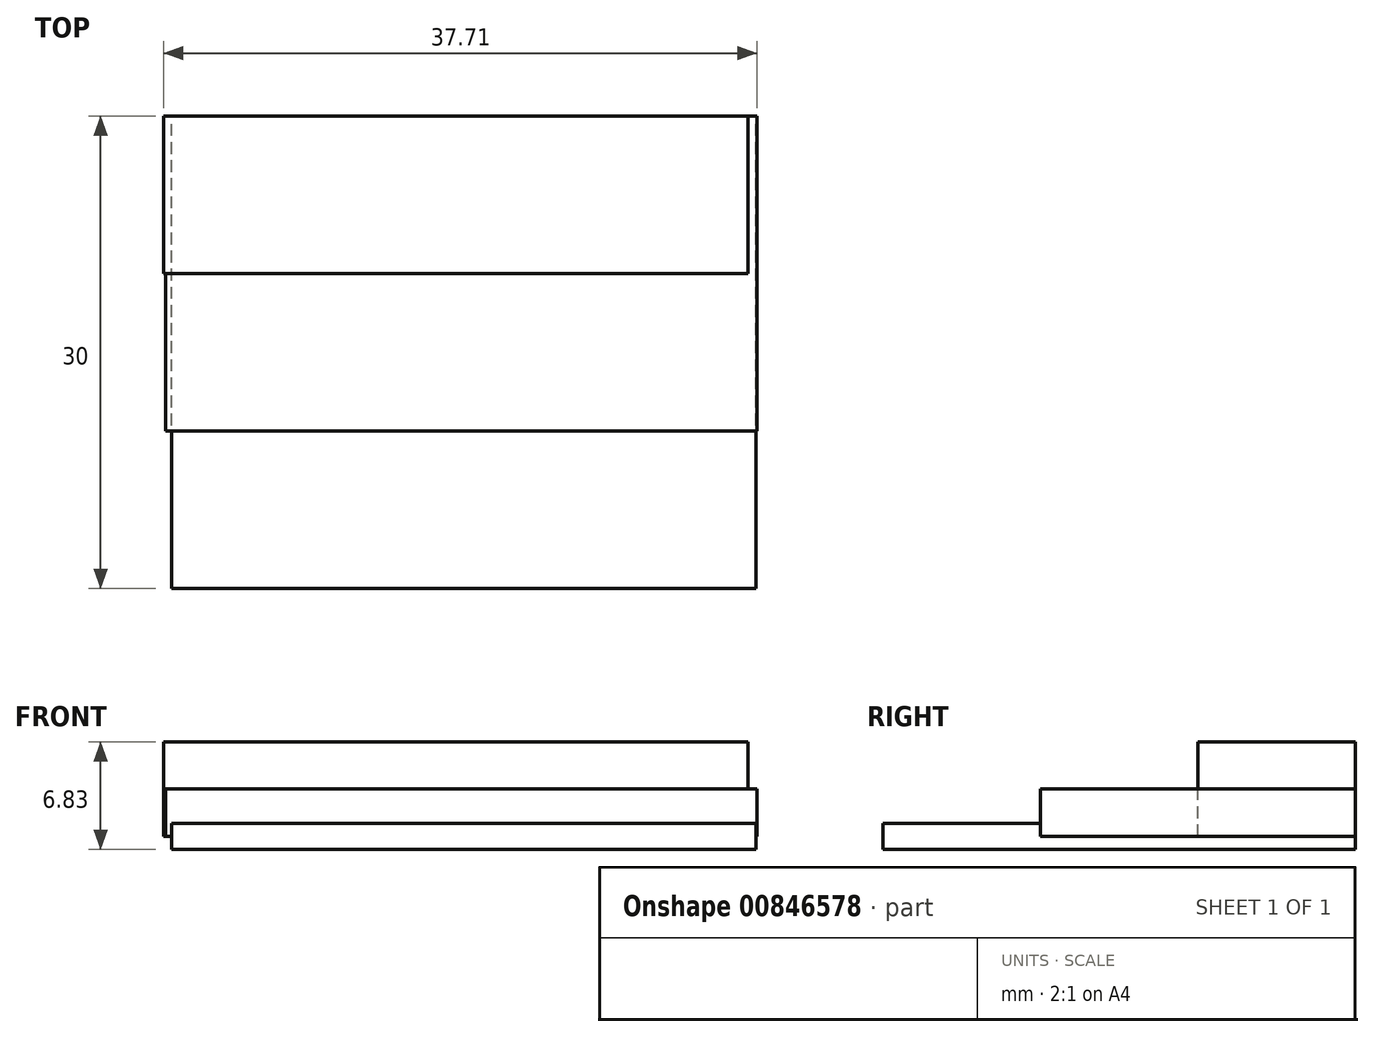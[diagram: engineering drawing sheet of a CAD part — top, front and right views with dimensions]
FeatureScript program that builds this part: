
annotation { "Feature Type Name" : "Feature", "Feature Type Description" : "" }
export const myFeature = defineFeature(function(context is Context, id is Id, definition is map)
    precondition{}
    {
        {
            var Q0;
            Q0=qCreatedBy(makeId("Front.planeOp"),FACE);
            var sketch = newSketch(context, id + "F0", { "sketchPlane" : qUnion([Q0])});
            skLineSegment(sketch, "E0.bottom", {"start": v(-15.71, 0.83) * mm, "end": v(21.43, 0.83) * mm});
            skLineSegment(sketch, "E0.top", {"start": v(-15.71, -0.83) * mm, "end": v(21.43, -0.83) * mm});
            skLineSegment(sketch, "E0.left", {"start": v(-15.71, 0.83) * mm, "end": v(-15.71, -0.83) * mm});
            skLineSegment(sketch, "E0.right", {"start": v(21.43, 0.83) * mm, "end": v(21.43, -0.83) * mm});
            skPoint(sketch, "E0.middle", {"position": v(2.86, 0) * mm});
            skSolve(sketch);
        }
        {
            var Q0;
            Q0 = qSketchRegion(id + "F0", true);
            extrude(context, id + "F1", {"entities" : qUnion([Q0]), "depth" : 30 * mm, "offsetDistance" : 25 * mm});
        }
        {
            var Q0;
            Q0=qCreatedBy(makeId("Top.planeOp"),FACE);
            var sketch = newSketch(context, id + "F2", { "sketchPlane" : qUnion([Q0])});
            skLineSegment(sketch, "E1", {"start": v(-16.08, 0) * mm, "end": v(21.5, 0) * mm});
            skLineSegment(sketch, "E2", {"start": v(21.5, 0) * mm, "end": v(21.5, -20) * mm});
            skLineSegment(sketch, "E3", {"start": v(21.5, -20) * mm, "end": v(-16.08, -20) * mm});
            skLineSegment(sketch, "E4", {"start": v(-16.08, -20) * mm, "end": v(-16.08, 0) * mm});
            skSolve(sketch);
        }
        {
            var Q0;
            Q0 = qSketchRegion(id + "F2", true);
            extrude(context, id + "F3", {"entities" : qUnion([Q0]), "operationType" : NewBodyOperationType.ADD, "depth" : 3 * mm, "offsetDistance" : 25 * mm});
        }
        {
            var Q0;
            Q0=qCreatedBy(makeId("Top.planeOp"),FACE);
            var sketch = newSketch(context, id + "F4", { "sketchPlane" : qUnion([Q0])});
            skLineSegment(sketch, "E5", {"start": v(-16.22, 0) * mm, "end": v(20.91, 0) * mm});
            skLineSegment(sketch, "E6", {"start": v(20.91, 0) * mm, "end": v(20.91, -10) * mm});
            skLineSegment(sketch, "E7", {"start": v(20.91, -10) * mm, "end": v(-16.22, -10) * mm});
            skLineSegment(sketch, "E8", {"start": v(-16.22, -10) * mm, "end": v(-16.22, 0) * mm});
            skSolve(sketch);
        }
        {
            var Q0;
            Q0 = qSketchRegion(id + "F4", true);
            extrude(context, id + "F5", {"entities" : qUnion([Q0]), "operationType" : NewBodyOperationType.ADD, "depth" : 6 * mm, "offsetDistance" : 25 * mm});
        }
    });
